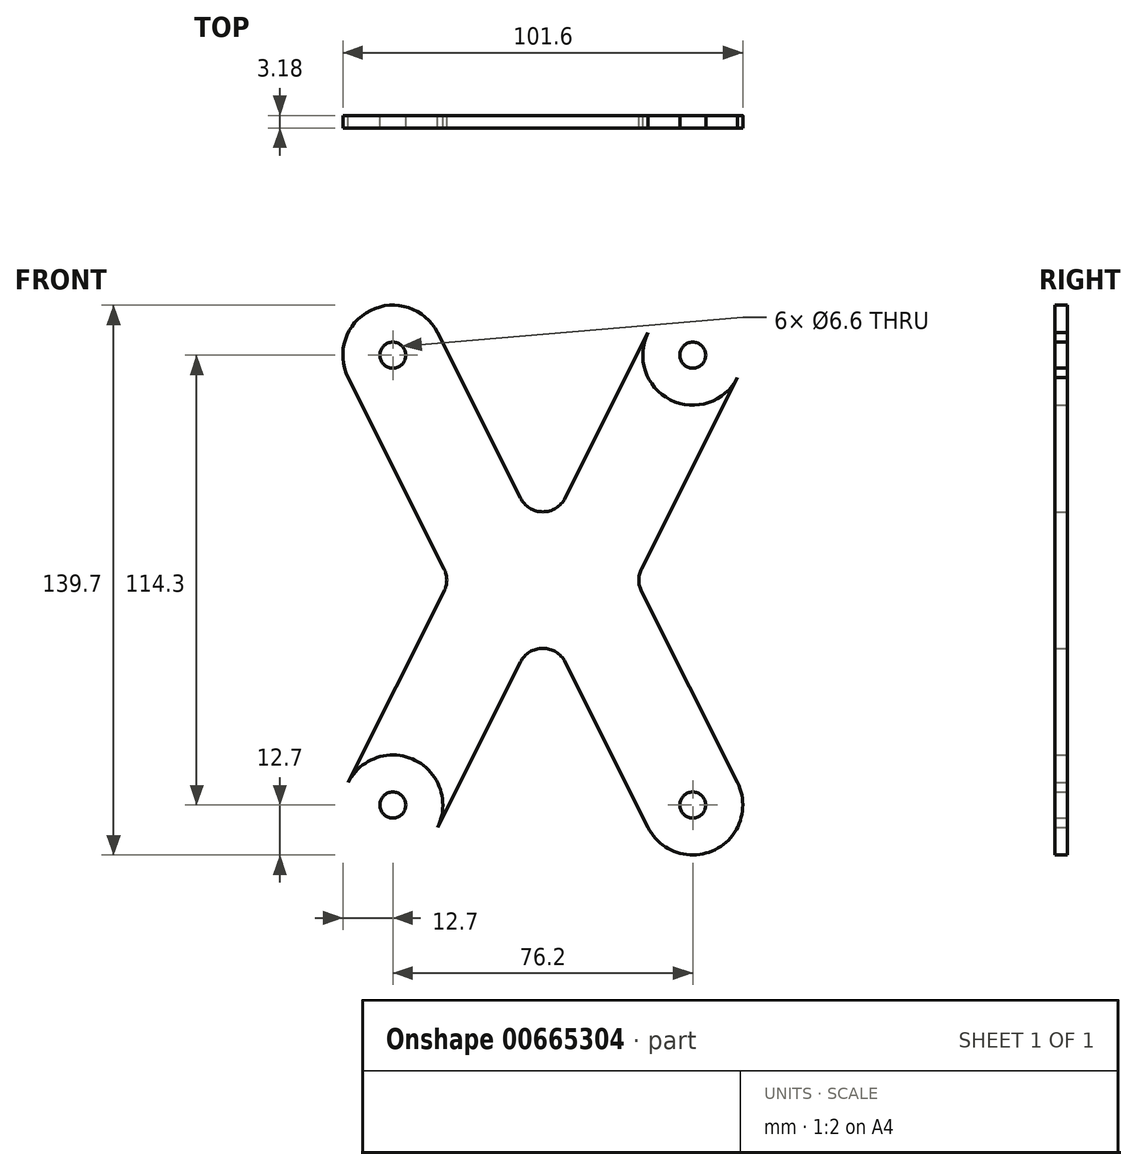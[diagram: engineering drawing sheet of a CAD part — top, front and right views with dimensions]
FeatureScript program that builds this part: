
annotation { "Feature Type Name" : "Feature", "Feature Type Description" : "" }
export const myFeature = defineFeature(function(context is Context, id is Id, definition is map)
    precondition{}
    {
        {
            var Q0;
            Q0=qCreatedBy(makeId("Front.planeOp"),FACE);
            var sketch = newSketch(context, id + "F0", { "sketchPlane" : qUnion([Q0])});
            skCircle(sketch, "E0", {"center": v(-38.1, 57.15) * mm, "radius": 3.3 * mm});
            skCircle(sketch, "E1.MirrorC", {"center": v(38.1, 57.15) * mm, "radius": 3.3 * mm});
            skCircle(sketch, "E2.MirrorC", {"center": v(-38.1, -57.15) * mm, "radius": 3.3 * mm});
            skCircle(sketch, "E3.MirrorC", {"center": v(38.1, -57.15) * mm, "radius": 3.3 * mm});
            skCircle(sketch, "E4", {"center": v(-38.1, 57.15) * mm, "radius": 12.7 * mm});
            skCircle(sketch, "E5", {"center": v(38.1, 57.15) * mm, "radius": 12.7 * mm});
            skCircle(sketch, "E6", {"center": v(38.1, -57.15) * mm, "radius": 12.7 * mm});
            skCircle(sketch, "E7", {"center": v(-38.1, -57.15) * mm, "radius": 12.7 * mm});
            skLineSegment(sketch, "E8", {"start": v(23.64, 0) * mm, "end": v(-23.64, 0) * mm, "construction": true});
            skPoint(sketch, "E9", {"position": v(0, 0) * mm});
            skLineSegment(sketch, "E10", {"start": v(0, 9.52) * mm, "end": v(0, -9.53) * mm, "construction": true});
            skLineSegment(sketch, "E11", {"start": v(-25.07, 2.85) * mm, "end": v(-49.45, 51.46) * mm});
            skLineSegment(sketch, "E12", {"start": v(-5.68, 20.84) * mm, "end": v(-26.75, 62.84) * mm});
            skLineSegment(sketch, "E13", {"start": v(5.68, 20.84) * mm, "end": v(26.75, 62.84) * mm});
            skLineSegment(sketch, "E14", {"start": v(25.07, 2.85) * mm, "end": v(49.45, 51.46) * mm});
            skLineSegment(sketch, "E15", {"start": v(25.07, -2.85) * mm, "end": v(49.45, -51.46) * mm});
            skLineSegment(sketch, "E16", {"start": v(5.68, -20.84) * mm, "end": v(26.75, -62.84) * mm});
            skLineSegment(sketch, "E17", {"start": v(-5.68, -20.84) * mm, "end": v(-26.75, -62.84) * mm});
            skLineSegment(sketch, "E18", {"start": v(-25.07, -2.85) * mm, "end": v(-49.45, -51.46) * mm});
            skPoint(sketch, "E19.visualSharp", {"position": v(0, 9.52) * mm});
            skArc(sketch, "E19.filletArc", {"start": v(-5.68, 20.84) * mm, "mid": v(0, 17.34) * mm, "end": v(5.68, 20.84) * mm});
            skPoint(sketch, "E20.visualSharp", {"position": v(-23.64, 0) * mm});
            skArc(sketch, "E20.filletArc", {"start": v(-25.07, -2.85) * mm, "mid": v(-24.4, 0) * mm, "end": v(-25.07, 2.85) * mm});
            skPoint(sketch, "E21.visualSharp", {"position": v(23.64, 0) * mm});
            skArc(sketch, "E21.filletArc", {"start": v(25.07, 2.85) * mm, "mid": v(24.4, 0) * mm, "end": v(25.07, -2.85) * mm});
            skPoint(sketch, "E22.visualSharp", {"position": v(0, -9.53) * mm});
            skArc(sketch, "E22.filletArc", {"start": v(5.68, -20.84) * mm, "mid": v(0, -17.34) * mm, "end": v(-5.68, -20.84) * mm});
            skSolve(sketch);
        }
        {
            var Q0;
            {var subQ3=sQuery(id+"F0.wireOp",EDGE,"E11");Q0=makeQuery(id+"F0.imprint","IMPRINT",FACE,{"disambiguationData":[TD([[makeQuery(id+"F0.imprint","IMPRINT",EDGE,{"derivedFrom":subQ3}),-1.0]])]});}
            var Q1;
            Q1=makeQuery(id+"F0.imprint","IMPRINT",FACE,{"disambiguationData":[TD([[makeQuery(id+"F0.imprint","IMPRINT",EDGE,{"derivedFrom":sQuery(id+"F0.wireOp",EDGE,"E0")}),-1.0]])]});
            var Q2;
            Q2=makeQuery(id+"F0.imprint","IMPRINT",FACE,{"disambiguationData":[TD([[makeQuery(id+"F0.imprint","IMPRINT",EDGE,{"derivedFrom":sQuery(id+"F0.wireOp",EDGE,"E1.MirrorC")}),1.0]])]});
            var Q3;
            Q3=makeQuery(id+"F0.imprint","IMPRINT",FACE,{"disambiguationData":[TD([[makeQuery(id+"F0.imprint","IMPRINT",EDGE,{"derivedFrom":sQuery(id+"F0.wireOp",EDGE,"E3.MirrorC")}),-1.0]])]});
            var Q4;
            Q4=makeQuery(id+"F0.imprint","IMPRINT",FACE,{"disambiguationData":[TD([[makeQuery(id+"F0.imprint","IMPRINT",EDGE,{"derivedFrom":sQuery(id+"F0.wireOp",EDGE,"E2.MirrorC")}),1.0]])]});
            extrude(context, id + "F1", {"entities" : qUnion([Q0, Q1, Q2, Q3, Q4]), "depth" : 3.17 * mm, "offsetDistance" : 25.4 * mm});
        }
    });
